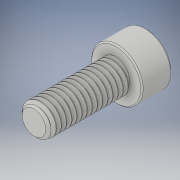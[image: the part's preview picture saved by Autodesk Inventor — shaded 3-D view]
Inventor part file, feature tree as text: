
AUTODESK INVENTOR PART (.ipt)
format: ipt  version: 2018 (Build 220112000, 112)  size: 773,120 bytes
history: native  units: in
note: dims shown in document units (in); Inventor stores cm internally (conversion verified against a paired STEP export)
features: chamfer x1
ambient origin geometry x8: Origin, YZ Plane, XZ Plane, XY Plane, X Axis, Y Axis, Z Axis, Center Point
bodies: Solid1 (feature_tree)
feature tree (1):
  chamfer  "Chamfer2"  [1 undecoded]
note: 1 required parameter value undecoded (feature->parameter linkage not recoverable at this tier; creation-order binding heuristic only, values carry confidence <= 0.55)
